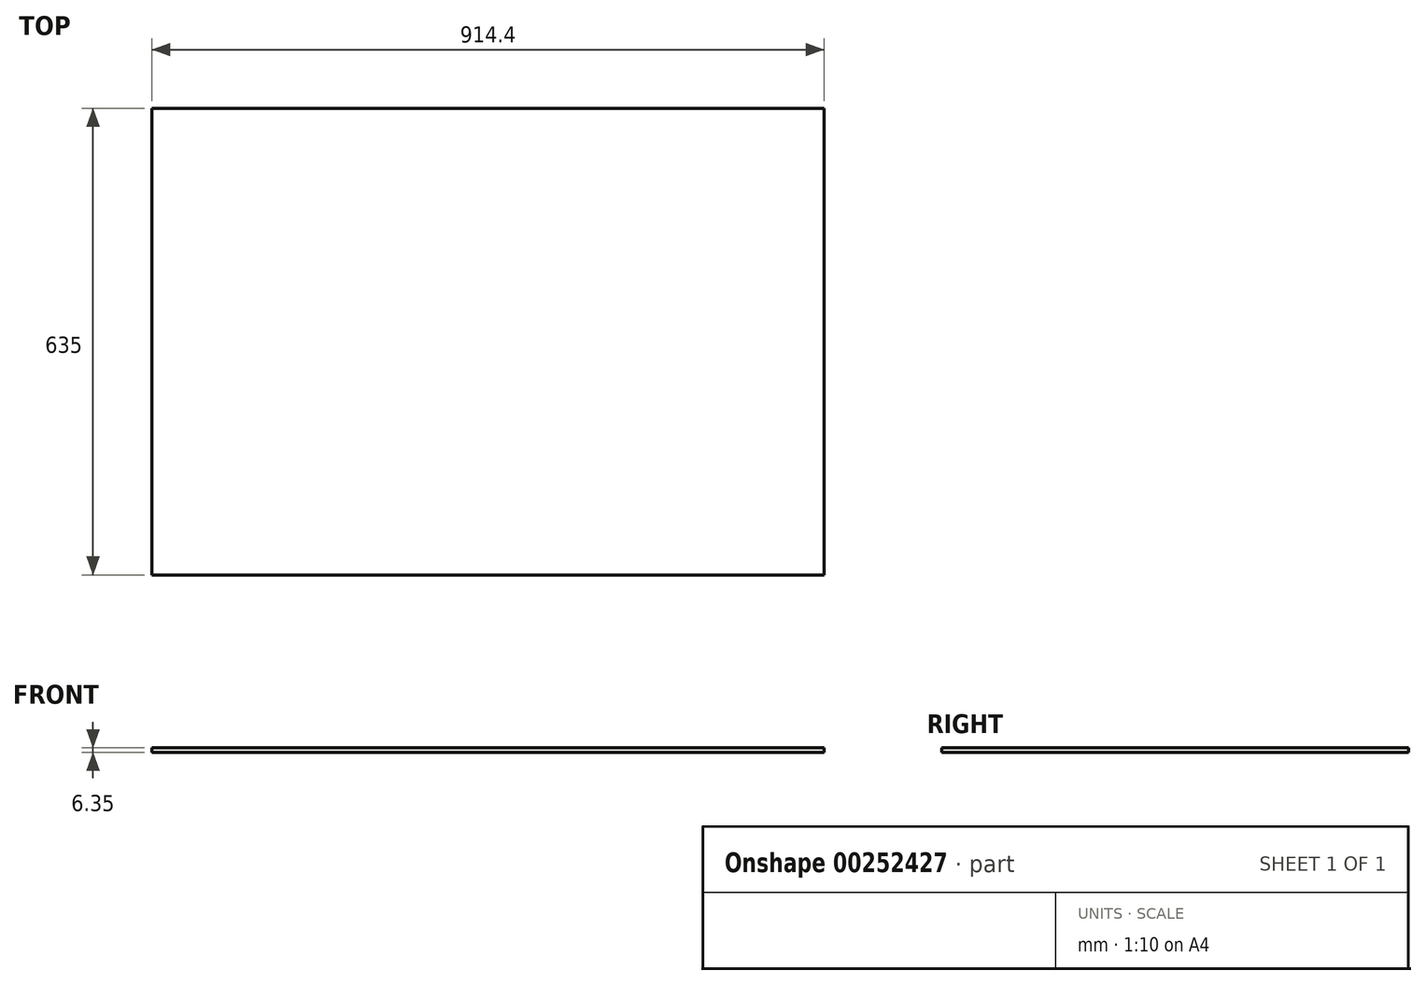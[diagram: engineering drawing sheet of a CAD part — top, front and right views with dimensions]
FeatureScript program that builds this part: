
annotation { "Feature Type Name" : "Feature", "Feature Type Description" : "" }
export const myFeature = defineFeature(function(context is Context, id is Id, definition is map)
    precondition{}
    {
        {
            var Q0;
            Q0=qCreatedBy(makeId("Top.planeOp"),FACE);
            var sketch = newSketch(context, id + "F0", { "sketchPlane" : qUnion([Q0])});
            skLineSegment(sketch, "E0.bottom", {"start": v(-457.2, 317.5) * mm, "end": v(457.2, 317.5) * mm});
            skLineSegment(sketch, "E0.top", {"start": v(-457.2, -317.5) * mm, "end": v(457.2, -317.5) * mm});
            skLineSegment(sketch, "E0.left", {"start": v(-457.2, 317.5) * mm, "end": v(-457.2, -317.5) * mm});
            skLineSegment(sketch, "E0.right", {"start": v(457.2, 317.5) * mm, "end": v(457.2, -317.5) * mm});
            skPoint(sketch, "E0.middle", {"position": v(0, 0) * mm});
            skSolve(sketch);
        }
        {
            var Q0;
            Q0=makeQuery(id+"F0.imprint","IMPRINT",FACE,{"disambiguationData":[TD([[makeQuery(id+"F0.imprint","IMPRINT",EDGE,{"derivedFrom":sQuery(id+"F0.wireOp",EDGE,"E0.bottom")}),-1.0]])]});
            extrude(context, id + "F1", {"entities" : qUnion([Q0]), "depth" : 6.35 * mm});
        }
    });
